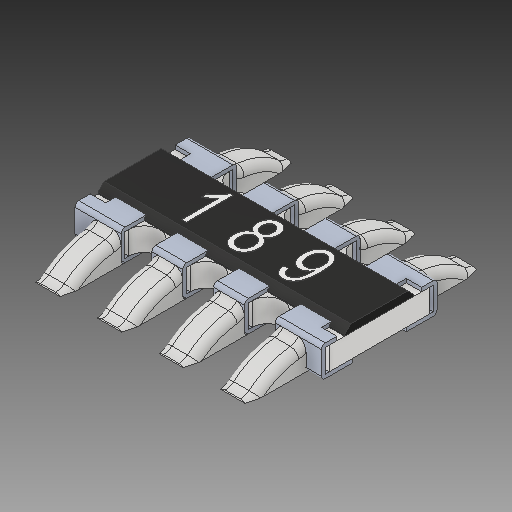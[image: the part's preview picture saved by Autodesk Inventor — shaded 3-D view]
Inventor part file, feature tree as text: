
AUTODESK INVENTOR PART (.ipt)
format: ipt  version: 2019 (Build 230136000, 136)  size: 609,280 bytes
history: native  units: in
note: dims shown in document units (in); Inventor stores cm internally (conversion verified against a paired STEP export)
features: other x8, fillet x2
ambient origin geometry x8: Origin, YZ Plane, XZ Plane, XY Plane, X Axis, Y Axis, Z Axis, Center Point
bodies: Solid1 (feature_tree), Solid2 (feature_tree), Solid3 (feature_tree), Solid4 (feature_tree), Solid5 (feature_tree), Solid6 (feature_tree), Solid7 (feature_tree), Solid8 (feature_tree), Solid9 (feature_tree), Solid10 (feature_tree)
feature tree (10):
  other  "Cut-Extrude7"
  other  "Boss-Extrude5"
  fillet  "Fillet2"  [1 undecoded]
  fillet  "Fillet1"  [1 undecoded]
  other  "LPattern3[1]"
  other  "LPattern3[2]"
  other  "LPattern3[3]"
  other  "LPattern3[4]"
  other  "LPattern3[5]"
  other  "LPattern3[6]"
note: 2 required parameter values undecoded (feature->parameter linkage not recoverable at this tier; creation-order binding heuristic only, values carry confidence <= 0.55)
